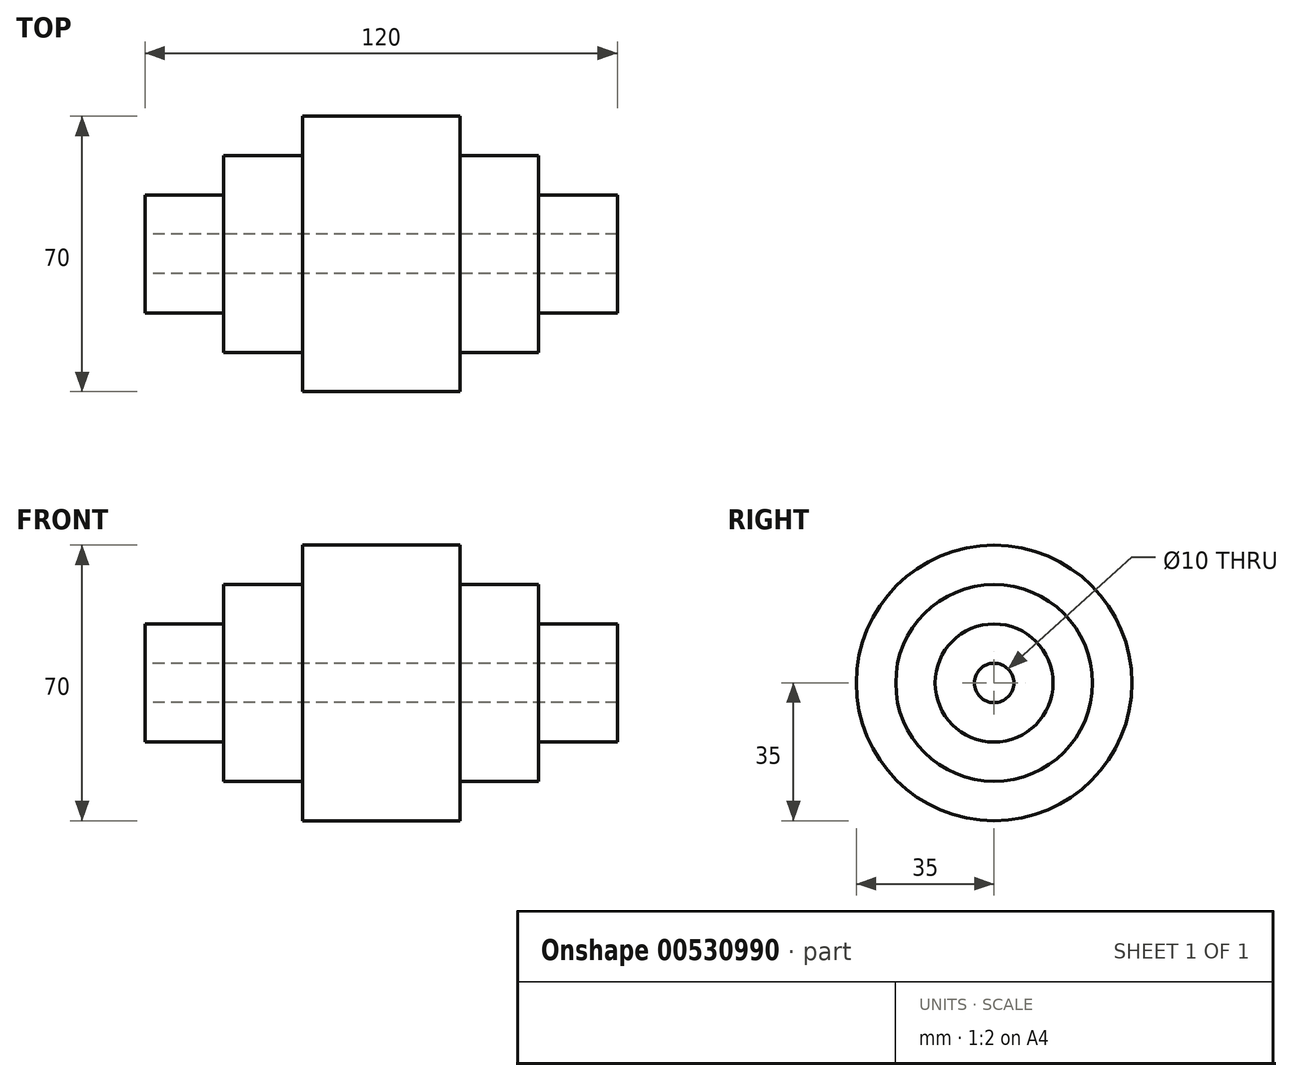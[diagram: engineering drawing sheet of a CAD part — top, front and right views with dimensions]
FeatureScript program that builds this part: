
annotation { "Feature Type Name" : "Feature", "Feature Type Description" : "" }
export const myFeature = defineFeature(function(context is Context, id is Id, definition is map)
    precondition{}
    {
        {
            var Q0;
            Q0=qCreatedBy(makeId("Front.planeOp"),FACE);
            var sketch = newSketch(context, id + "F0", { "sketchPlane" : qUnion([Q0])});
            skLineSegment(sketch, "E0.bottom", {"start": v(0, 35) * mm, "end": v(20, 35) * mm});
            skLineSegment(sketch, "E0.top", {"start": v(0, 5) * mm, "end": v(20, 5) * mm});
            skLineSegment(sketch, "E0.left", {"start": v(0, 35) * mm, "end": v(0, 5) * mm});
            skLineSegment(sketch, "E0.right", {"start": v(20, 35) * mm, "end": v(20, 25) * mm});
            skLineSegment(sketch, "E1.bottom", {"start": v(20, 25) * mm, "end": v(40, 25) * mm});
            skLineSegment(sketch, "E1.top", {"start": v(13.3, 5) * mm, "end": v(40, 5) * mm});
            skLineSegment(sketch, "E1.right", {"start": v(40, 25) * mm, "end": v(40, 15) * mm});
            skLineSegment(sketch, "E2.bottom", {"start": v(40, 15) * mm, "end": v(60, 15) * mm});
            skLineSegment(sketch, "E2.top", {"start": v(24.38, 5) * mm, "end": v(60, 5) * mm});
            skLineSegment(sketch, "E2.right", {"start": v(60, 15) * mm, "end": v(60, 5) * mm});
            skLineSegment(sketch, "E3", {"start": v(-37.63, 0) * mm, "end": v(83.22, 0) * mm, "construction": true});
            skSolve(sketch);
        }
        {
            var Q0;
            Q0=makeQuery(id+"F0.imprint","IMPRINT",FACE,{"disambiguationData":[TD([[makeQuery(id+"F0.imprint","IMPRINT",EDGE,{"derivedFrom":sQuery(id+"F0.wireOp",EDGE,"E0.bottom")}),-1.0]])]});
            var Q1;
            Q1=sQuery(id+"F0.wireOp",EDGE,"E3");
            revolve(context, id + "F1", {"surfaceOperationType" : NewSurfaceOperationType.NEW, "entities" : qUnion([Q0]), "axis" : qUnion([Q1]), "revolveType" : RevolveType.FULL});
        }
        {
            var Q0;
            Q0=makeQuery(id+"F1.opRevolve","SWEPT_BODY",BODY,{"disambiguationData":[OSD([sQuery(id+"F0.wireOp",EDGE,"E0.bottom"),sQuery(id+"F0.wireOp",EDGE,"E0.top"),sQuery(id+"F0.wireOp",EDGE,"E0.left"),sQuery(id+"F0.wireOp",EDGE,"E0.right"),sQuery(id+"F0.wireOp",EDGE,"E1.bottom"),sQuery(id+"F0.wireOp",EDGE,"E1.top"),sQuery(id+"F0.wireOp",EDGE,"E1.right"),sQuery(id+"F0.wireOp",EDGE,"E2.bottom"),sQuery(id+"F0.wireOp",EDGE,"E2.top"),sQuery(id+"F0.wireOp",EDGE,"E2.right")])]});
            var Q1;
            Q1=qCreatedBy(makeId("Right.planeOp"),FACE);
            mirror(context, id + "F2", {"operationType" : NewBodyOperationType.ADD, "entities" : qUnion([Q0]), "mirrorPlane" : qUnion([Q1])});
        }
    });
